# Revit family: Gira_134228
name_source: partatom
category: Electrical Fixtures
revit_build: Autodesk Revit 2017 (Build: 20160225_1515(x64)
units: mm (PartAtom-declared; Revit-internal decimal feet)

## family parameters
Cut with Voids When Loaded = No
Host = Face
Maintain Annotation Orientation = Yes
Part Type = Normal
Room Calculation Point = No
Round Connector Dimension = Use Diameter
Shared = No

## types (1)
- En.prof. light + 3x SCHUKO SH 769 mm Gira energy profile anthra.
    Available = No
    BIM (1) = https://media.stage.bim.site
    Category = Light/energy pole
    Data sheet (1) = https://katalog.gira.de
    Default Elevation = 1219 mm
    Depth = 0,075
    Description = 769 mm light 3x SCHUKO SH E-pro AN,Gira energy profile with light element, height 769 mm,3 SCHUKO socket outlets with integrated enhanced contact protection (shutter) and symbol ,anthracite,Gira energy profile and light profiles with or without light elements for outdoor use. The profiles are made of powder-coated aluminium. For profiles of up to 1400 mm, the base elements are also made of powder-coated aluminium. For profiles of 1400 mm or more, the base elements are made of powder-coated steel. In each case, in the colour anthracite in accordance with the GSB standard. The surface is resistant to weather, UV, soiling, and scratching.,,Features:,- Gira energy profile with light element and three SCHUKO socket outlets.,- The light element consists of an aluminium reflector and an impact-resistant acrylic glass plate.,- Light is also emitted from the rear as orientation light.,- The top two socket outlets are rotated by 30.,- The connection is made using a 5-pole screw terminal for rigid and flexible conductors up to 4 mm 2.,,Notes :,- For profile heights up to 1400 mm, an optional ground anchor can be used to facilitate mounting on a stone or concrete base.,- For profile heights of more than 1400 mm, mounting on stone or concrete is only possible using 3 heavy-duty wall anchor.,- Recommendation: Mount an RCCB prior to the device.,- Single-wall plug mounting.,- Increased contact protection pursuant to DIN-VDE 0620-1.,- Light sources with E27 treading of the energy efficiency classes A++ to E can be used.
    GTIN = 4010337342281
    HAN = 134228
    Height = 0,769
    HeinzeBIM = https://bimportal.heinze.de
    Manufacturer = Gira
    Manufacturer URL = https://www.gira.de
    Name = En.prof. light + 3x SCHUKO SH 769 mm Gira energy profile anthra.
    Number of socket outlets = 2
    Switching function = None
    URL = http://katalog.gira.de
    Width = 0,142

## geometry (parser evidence)
native form markers: Blend x2, Sweep x3
no freeform markers — native parametric forms only
